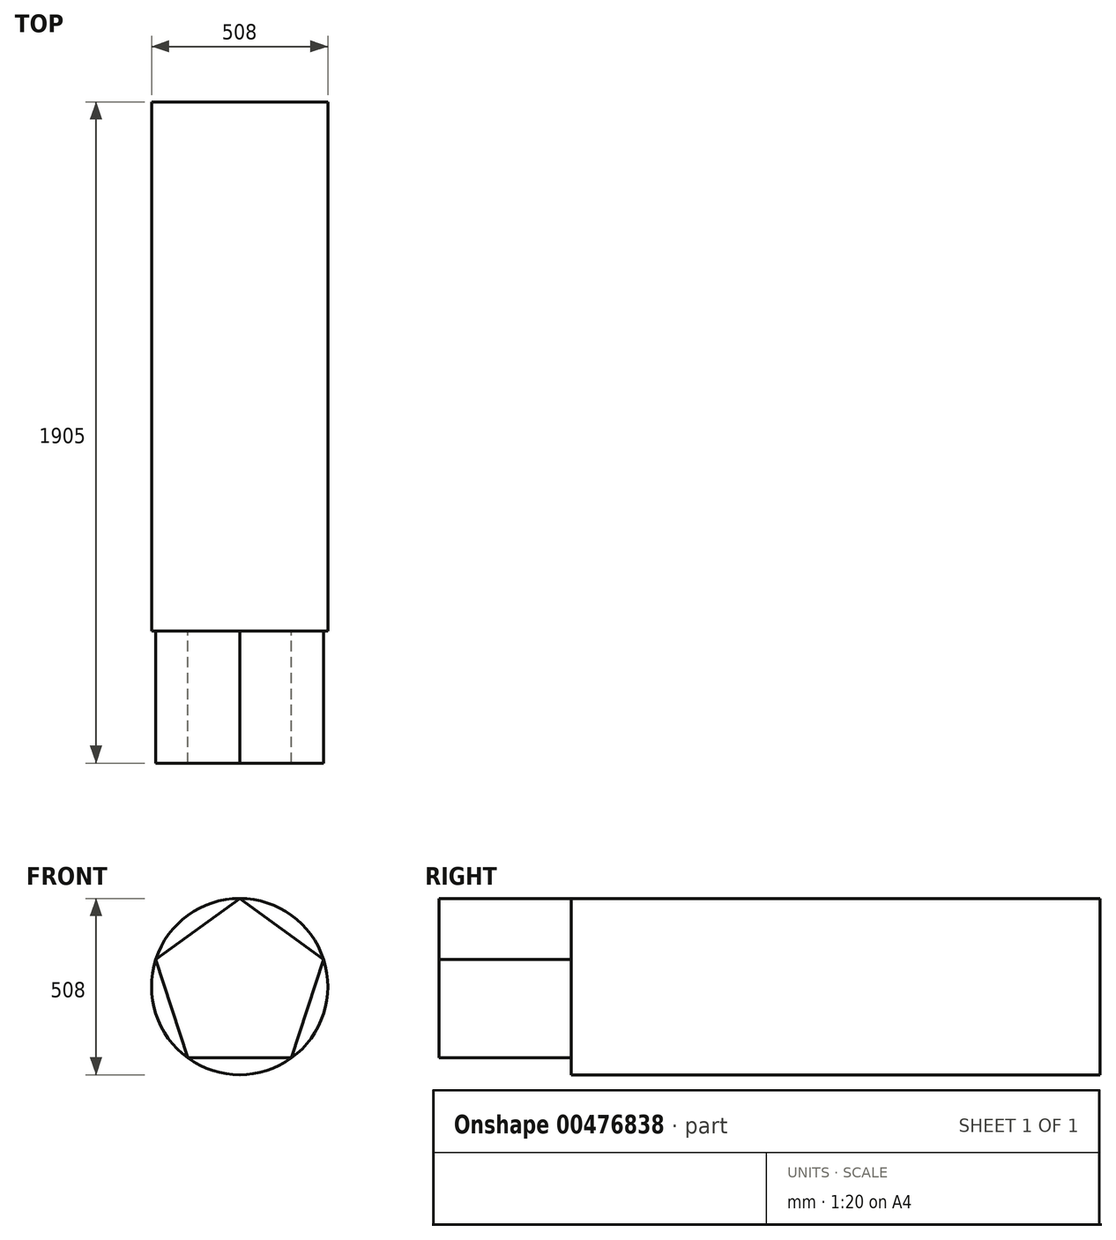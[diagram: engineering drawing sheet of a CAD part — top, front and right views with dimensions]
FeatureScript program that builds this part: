
annotation { "Feature Type Name" : "Feature", "Feature Type Description" : "" }
export const myFeature = defineFeature(function(context is Context, id is Id, definition is map)
    precondition{}
    {
        {
            var Q0;
            Q0=qCreatedBy(makeId("Front.planeOp"),FACE);
            var sketch = newSketch(context, id + "F0", { "sketchPlane" : qUnion([Q0])});
            skCircle(sketch, "E0", {"center": v(0, 0) * mm, "radius": 254 * mm});
            skSolve(sketch);
        }
        {
            var Q0;
            Q0 = qSketchRegion(id + "F0", true);
            extrude(context, id + "F1", {"entities" : qUnion([Q0]), "depth" : 1524 * mm});
        }
        {
            var Q0;
            Q0=makeQuery(id+"F1.opExtrude","CAP_FACE",FACE,{"disambiguationData":[OSD([sQuery(id+"F0.wireOp",EDGE,"E0")])],"isStart":false});
            var sketch = newSketch(context, id + "F2", { "sketchPlane" : qUnion([Q0])});
            skCircle(sketch, "E1.cCircle", {"center": v(0, 0) * mm, "radius": 254 * mm, "construction": true});
            skLineSegment(sketch, "E1.0", {"start": v(0, 254) * mm, "end": v(241.57, 78.5) * mm});
            skLineSegment(sketch, "E1.1", {"start": v(241.57, 78.5) * mm, "end": v(149.3, -205.5) * mm});
            skLineSegment(sketch, "E1.2", {"start": v(149.3, -205.5) * mm, "end": v(-149.3, -205.5) * mm});
            skLineSegment(sketch, "E1.3", {"start": v(-149.3, -205.5) * mm, "end": v(-241.57, 78.5) * mm});
            skLineSegment(sketch, "E1.4", {"start": v(-241.57, 78.5) * mm, "end": v(0, 254) * mm});
            skSolve(sketch);
        }
        {
            var Q0;
            Q0 = qSketchRegion(id + "F2", true);
            extrude(context, id + "F3", {"entities" : qUnion([Q0]), "operationType" : NewBodyOperationType.ADD, "depth" : 381 * mm});
        }
    });
